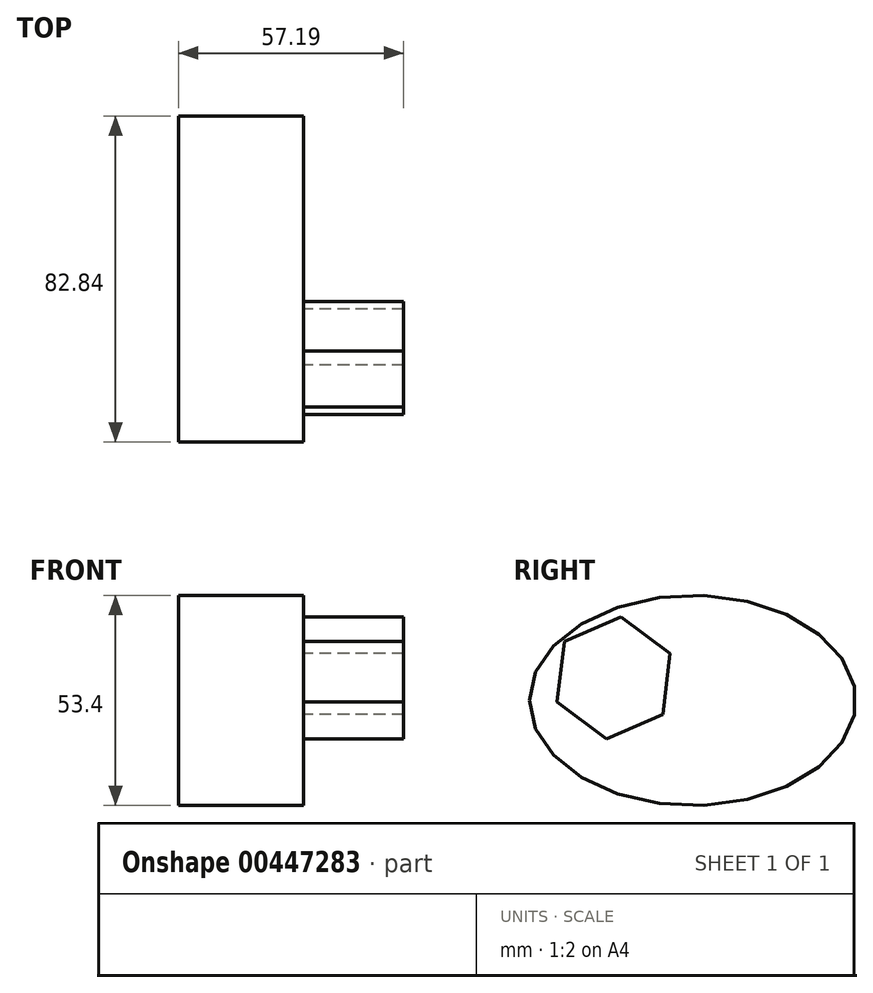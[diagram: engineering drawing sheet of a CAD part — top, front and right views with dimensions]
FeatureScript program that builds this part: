
annotation { "Feature Type Name" : "Feature", "Feature Type Description" : "" }
export const myFeature = defineFeature(function(context is Context, id is Id, definition is map)
    precondition{}
    {
        {
            var Q0;
            Q0=qCreatedBy(makeId("Right.planeOp"),FACE);
            var sketch = newSketch(context, id + "F0", { "sketchPlane" : qUnion([Q0])});
            skEllipse(sketch, "E0", {"center": v(0, 0) * mm, "majorRadius": 41.42 * mm, "minorRadius": 26.7 * mm, "majorAxis": v(-1, 0)});
            skSolve(sketch);
        }
        {
            var Q0;
            Q0 = qSketchRegion(id + "F0", true);
            extrude(context, id + "F1", {"entities" : qUnion([Q0]), "depth" : 31.8 * mm});
        }
        {
            var Q0;
            Q0=makeQuery(id+"F1.opExtrude","CAP_FACE",FACE,{"disambiguationData":[OSD([sQuery(id+"F0.wireOp",EDGE,"E0")])],"isStart":false});
            var sketch = newSketch(context, id + "F2", { "sketchPlane" : qUnion([Q0])});
            skSolve(sketch);
        }
        {
            var Q0;
            Q0=makeQuery(id+"F2.imprint","IMPRINT",FACE,{"disambiguationData":[TD([[makeQuery(id+"F2.imprint","IMPRINT",EDGE,{"derivedFrom":makeQuery(id+"F1.opExtrude","CAP_EDGE",EDGE,{"disambiguationData":[OSD([sQuery(id+"F0.wireOp",EDGE,"E0")])],"isStart":false})}),1.0]])]});
            var sketch = newSketch(context, id + "F3", { "sketchPlane" : qUnion([Q0])});
            skCircle(sketch, "E1.cCircle", {"center": v(-20.1, 5.75) * mm, "radius": 15.58 * mm, "construction": true});
            skLineSegment(sketch, "E1.0", {"start": v(-21.92, -9.72) * mm, "end": v(-34.4, -0.4) * mm});
            skLineSegment(sketch, "E1.1", {"start": v(-34.4, -0.4) * mm, "end": v(-32.58, 15.07) * mm});
            skLineSegment(sketch, "E1.2", {"start": v(-32.58, 15.07) * mm, "end": v(-18.26, 21.22) * mm});
            skLineSegment(sketch, "E1.3", {"start": v(-18.26, 21.22) * mm, "end": v(-5.78, 11.9) * mm});
            skLineSegment(sketch, "E1.4", {"start": v(-5.78, 11.9) * mm, "end": v(-7.6, -3.57) * mm});
            skLineSegment(sketch, "E1.5", {"start": v(-7.6, -3.57) * mm, "end": v(-21.92, -9.72) * mm});
            skSolve(sketch);
        }
        {
            var Q0;
            Q0 = qSketchRegion(id + "F3", true);
            extrude(context, id + "F4", {"entities" : qUnion([Q0]), "operationType" : NewBodyOperationType.ADD, "depth" : 25.4 * mm});
        }
    });
